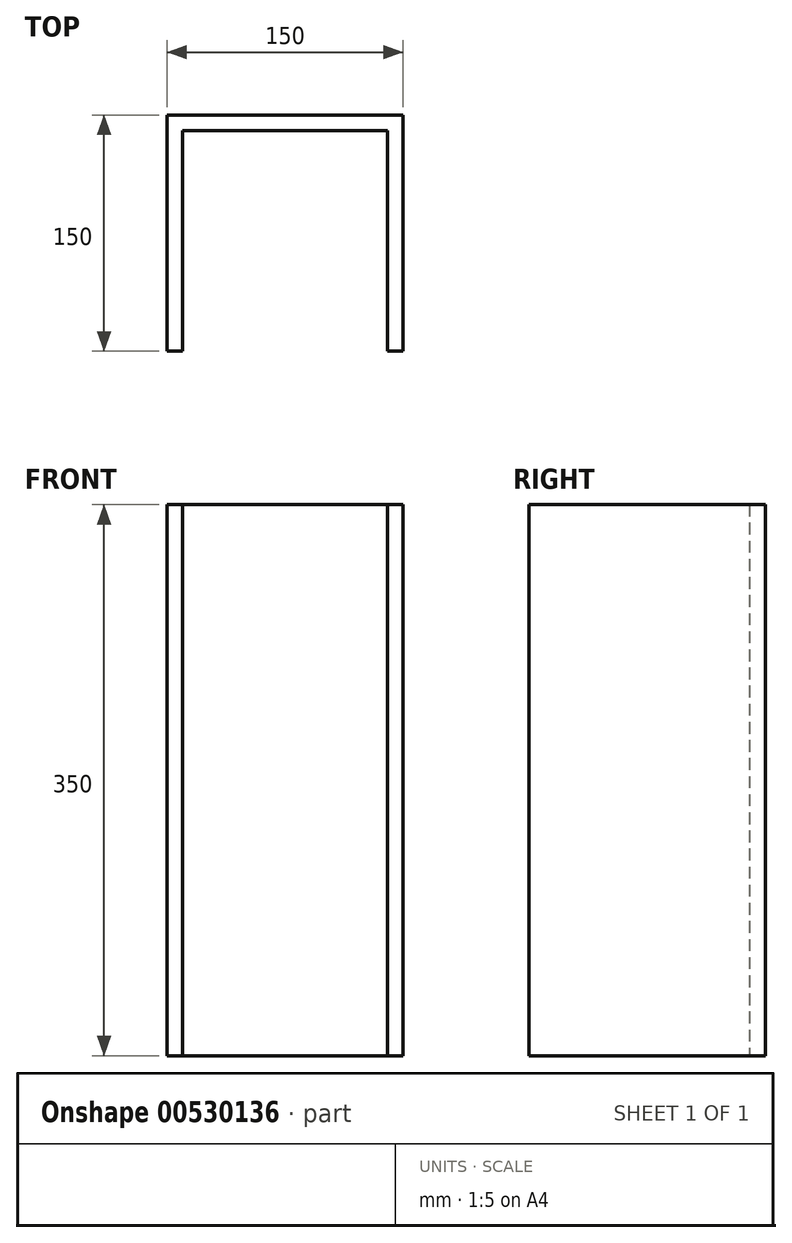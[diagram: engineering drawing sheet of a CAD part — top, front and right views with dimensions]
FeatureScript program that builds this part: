
annotation { "Feature Type Name" : "Feature", "Feature Type Description" : "" }
export const myFeature = defineFeature(function(context is Context, id is Id, definition is map)
    precondition{}
    {
        {
            var Q0;
            Q0=qCreatedBy(makeId("Top.planeOp"),FACE);
            var sketch = newSketch(context, id + "F0", { "sketchPlane" : qUnion([Q0])});
            skLineSegment(sketch, "E0.left", {"start": v(100, -100) * mm, "end": v(100, 50) * mm});
            skLineSegment(sketch, "E0.right", {"start": v(-50, -100) * mm, "end": v(-50, 50) * mm});
            skPoint(sketch, "E0.middle", {"position": v(0, 0) * mm});
            skLineSegment(sketch, "E1", {"start": v(-50, 50) * mm, "end": v(100, 50) * mm});
            skLineSegment(sketch, "E2.0", {"start": v(90, -100) * mm, "end": v(90, 40) * mm});
            skLineSegment(sketch, "E2.1", {"start": v(-40, 40) * mm, "end": v(90, 40) * mm});
            skLineSegment(sketch, "E2.2", {"start": v(-40, -100) * mm, "end": v(-40, 40) * mm});
            skLineSegment(sketch, "E3", {"start": v(-50, -100) * mm, "end": v(-40, -100) * mm});
            skLineSegment(sketch, "E4", {"start": v(90, -100) * mm, "end": v(100, -100) * mm});
            skSolve(sketch);
        }
        {
            var Q0;
            Q0=makeQuery(id+"F0.imprint","IMPRINT",FACE,{"disambiguationData":[TD([[makeQuery(id+"F0.imprint","IMPRINT",EDGE,{"derivedFrom":sQuery(id+"F0.wireOp",EDGE,"E0.left")}),1.0]])]});
            extrude(context, id + "F1", {"entities" : qUnion([Q0]), "depth" : 350 * mm, "offsetDistance" : 25 * mm});
        }
    });
